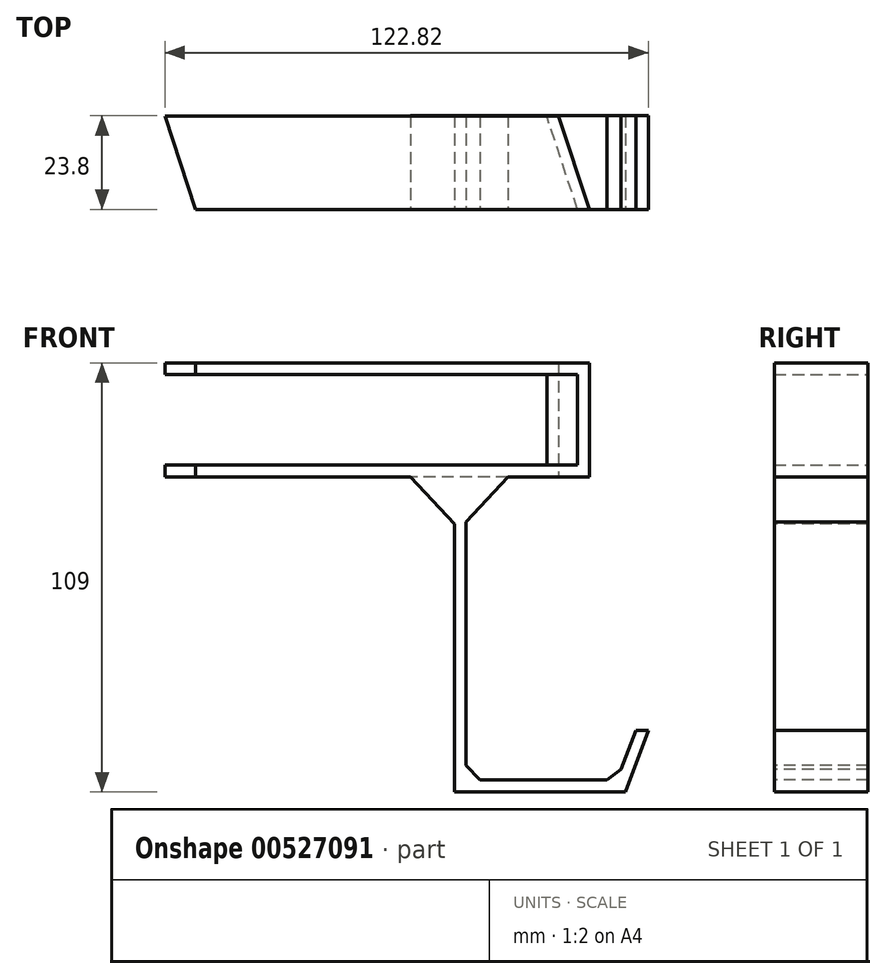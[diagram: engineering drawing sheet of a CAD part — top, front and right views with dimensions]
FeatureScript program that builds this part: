
annotation { "Feature Type Name" : "Feature", "Feature Type Description" : "" }
export const myFeature = defineFeature(function(context is Context, id is Id, definition is map)
    precondition{}
    {
        {
            var Q0;
            Q0=qCreatedBy(makeId("Front.planeOp"),FACE);
            var sketch = newSketch(context, id + "F0", { "sketchPlane" : qUnion([Q0])});
            skLineSegment(sketch, "E0", {"start": v(0, 29) * mm, "end": v(100, 29) * mm});
            skLineSegment(sketch, "E1", {"start": v(100, 29) * mm, "end": v(100, 0) * mm});
            skLineSegment(sketch, "E2", {"start": v(100, 0) * mm, "end": v(0, 0) * mm});
            skLineSegment(sketch, "E3.0", {"start": v(97, 3) * mm, "end": v(0, 3) * mm});
            skLineSegment(sketch, "E3.1", {"start": v(97, 26) * mm, "end": v(97, 3) * mm});
            skLineSegment(sketch, "E3.2", {"start": v(0, 26) * mm, "end": v(97, 26) * mm});
            skLineSegment(sketch, "E4", {"start": v(0, 26) * mm, "end": v(0, 29) * mm});
            skLineSegment(sketch, "E5", {"start": v(0, 3) * mm, "end": v(0, 0) * mm});
            skSolve(sketch);
        }
        {
            var Q0;
            Q0=qCreatedBy(makeId("Top.planeOp"),FACE);
            var sketch = newSketch(context, id + "F1", { "sketchPlane" : qUnion([Q0])});
            skLineSegment(sketch, "E6", {"start": v(100, 0) * mm, "end": v(92.2, 23.75) * mm});
            skSolve(sketch);
        }
        {
            var Q0;
            Q0 = qSketchRegion(id + "F0", true);
            var Q1;
            Q1=sQuery(id+"F1.wireOp",EDGE,"E6");
            sweep(context, id + "F2", {"profiles" : qUnion([Q0]), "path" : qUnion([Q1])});
        }
        {
            var Q0;
            Q0=qCreatedBy(makeId("Front.planeOp"),FACE);
            var sketch = newSketch(context, id + "F3", { "sketchPlane" : qUnion([Q0])});
            skLineSegment(sketch, "E7.top", {"start": v(68.7, 0) * mm, "end": v(65.7, 0) * mm});
            skLineSegment(sketch, "E7.left", {"start": v(68.7, -77) * mm, "end": v(68.7, 0) * mm});
            skLineSegment(sketch, "E7.right", {"start": v(65.7, -80) * mm, "end": v(65.7, 0) * mm});
            skLineSegment(sketch, "E8", {"start": v(109.15, -80) * mm, "end": v(115, -64.45) * mm});
            skLineSegment(sketch, "E9", {"start": v(115, -64.45) * mm, "end": v(111.8, -64.45) * mm});
            skLineSegment(sketch, "E10", {"start": v(111.8, -64.45) * mm, "end": v(107.07, -77) * mm});
            skLineSegment(sketch, "E11", {"start": v(107.07, -77) * mm, "end": v(68.7, -77) * mm});
            skLineSegment(sketch, "E12", {"start": v(65.7, -80) * mm, "end": v(109.15, -80) * mm});
            skLineSegment(sketch, "E13", {"start": v(54.62, 0) * mm, "end": v(66.97, -13.33) * mm});
            skLineSegment(sketch, "E14", {"start": v(66.97, -13.33) * mm, "end": v(79.33, 0) * mm});
            skLineSegment(sketch, "E15", {"start": v(79.33, 0) * mm, "end": v(54.62, 0) * mm});
            skLineSegment(sketch, "E16", {"start": v(68.7, -73.24) * mm, "end": v(72.23, -77) * mm});
            skLineSegment(sketch, "E17", {"start": v(108.1, -74.27) * mm, "end": v(104.54, -77) * mm});
            skSolve(sketch);
        }
        {
            var Q0;
            Q0=makeQuery(id+"F3.imprint","IMPRINT",FACE,{"disambiguationData":[TD([[makeQuery(id+"F3.imprint","IMPRINT",EDGE,{"derivedFrom":sQuery(id+"F3.wireOp",EDGE,"E7.top")}),1.0]])]});
            var Q1;
            Q1=makeQuery(id+"F3.imprint","IMPRINT",FACE,{"disambiguationData":[TD([[makeQuery(id+"F3.imprint","IMPRINT",EDGE,{"derivedFrom":sQuery(id+"F3.wireOp",EDGE,"E8")}),1.0]])]});
            var Q2;
            {var subQ0=sQuery(id+"F3.wireOp",EDGE,"E15");var subQ1=sQuery(id+"F3.wireOp",EDGE,"E7.left");var subQ2=makeQuery(id+"F3.imprint","INTERSECT",VERTEX,{"derivedFrom":[subQ1,subQ0]});Q2=makeQuery(id+"F3.imprint","IMPRINT",FACE,{"disambiguationData":[TD([[makeQuery(id+"F3.imprint","IMPRINT",EDGE,{"disambiguationData":[TD([[subQ2,1.0]])],"derivedFrom":subQ1}),-1.0]])]});}
            var Q3;
            {var subQ0=sQuery(id+"F3.wireOp",EDGE,"E15");var subQ1=sQuery(id+"F3.wireOp",EDGE,"E7.right");var subQ2=makeQuery(id+"F3.imprint","INTERSECT",VERTEX,{"derivedFrom":[subQ1,subQ0]});Q3=makeQuery(id+"F3.imprint","IMPRINT",FACE,{"disambiguationData":[TD([[makeQuery(id+"F3.imprint","IMPRINT",EDGE,{"disambiguationData":[TD([[subQ2,1.0]])],"derivedFrom":subQ1}),1.0]])]});}
            var Q4;
            {var subQ5=sQuery(id+"F3.wireOp",EDGE,"E15");var subQ7=sQuery(id+"F3.wireOp",EDGE,"E7.left");var subQ8=makeQuery(id+"F3.imprint","INTERSECT",VERTEX,{"derivedFrom":[subQ7,subQ5]});Q4=makeQuery(id+"F3.imprint","IMPRINT",FACE,{"disambiguationData":[TD([[makeQuery(id+"F3.imprint","IMPRINT",EDGE,{"disambiguationData":[TD([[subQ8,1.0]])],"derivedFrom":subQ7}),1.0]])]});}
            var Q5;
            {var subQ3=sQuery(id+"F3.wireOp",EDGE,"E16");Q5=makeQuery(id+"F3.imprint","IMPRINT",FACE,{"disambiguationData":[TD([[makeQuery(id+"F3.imprint","IMPRINT",EDGE,{"derivedFrom":subQ3}),-1.0]])]});}
            var Q6;
            {var subQ3=sQuery(id+"F3.wireOp",EDGE,"E17");Q6=makeQuery(id+"F3.imprint","IMPRINT",FACE,{"disambiguationData":[TD([[makeQuery(id+"F3.imprint","IMPRINT",EDGE,{"derivedFrom":subQ3}),1.0]])]});}
            extrude(context, id + "F4", {"entities" : qUnion([Q0, Q1, Q2, Q3, Q4, Q5, Q6]), "operationType" : NewBodyOperationType.ADD, "oppositeDirection" : true, "depth" : 23.8 * mm, "offsetDistance" : 25 * mm});
        }
    });
